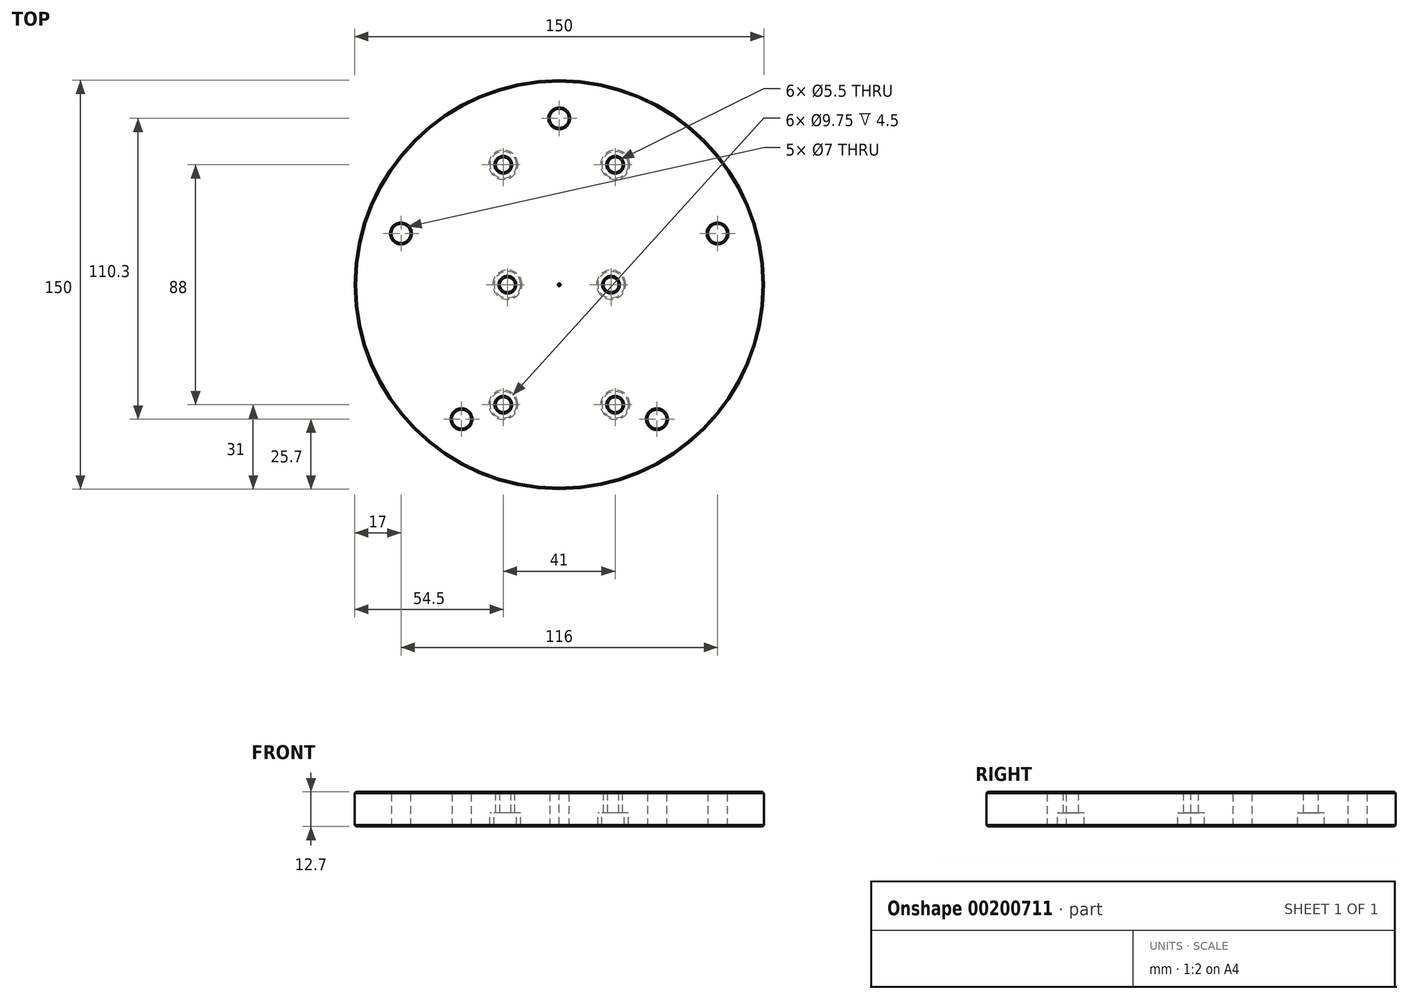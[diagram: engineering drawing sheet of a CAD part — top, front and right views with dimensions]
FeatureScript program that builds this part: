
annotation { "Feature Type Name" : "Feature", "Feature Type Description" : "" }
export const myFeature = defineFeature(function(context is Context, id is Id, definition is map)
    precondition{}
    {
        {
            var Q0;
            Q0=qCreatedBy(makeId("Top.planeOp"),FACE);
            var sketch = newSketch(context, id + "F0", { "sketchPlane" : qUnion([Q0])});
            skPoint(sketch, "E0.middle", {"position": v(0, 0) * mm});
            skCircle(sketch, "E1", {"center": v(0, 0) * mm, "radius": 75 * mm});
            skLineSegment(sketch, "E2.bottom", {"start": v(20.5, -44) * mm, "end": v(-20.5, -44) * mm, "construction": true});
            skLineSegment(sketch, "E2.top", {"start": v(20.5, 44) * mm, "end": v(-20.5, 44) * mm, "construction": true});
            skLineSegment(sketch, "E2.left", {"start": v(20.5, -44) * mm, "end": v(20.5, 44) * mm, "construction": true});
            skLineSegment(sketch, "E2.right", {"start": v(-20.5, -44) * mm, "end": v(-20.5, 44) * mm, "construction": true});
            skPoint(sketch, "E3", {"position": v(-20.5, 44) * mm});
            skPoint(sketch, "E4", {"position": v(20.5, 44) * mm});
            skPoint(sketch, "E5", {"position": v(-20.5, -44) * mm});
            skPoint(sketch, "E6", {"position": v(20.5, -44) * mm});
            skPoint(sketch, "E7", {"position": v(19, 0) * mm});
            skPoint(sketch, "E8", {"position": v(-19, 0) * mm});
            skSolve(sketch);
        }
        {
            var Q0;
            Q0=makeQuery(id+"F0.imprint","IMPRINT",FACE,{"disambiguationData":[TD([[makeQuery(id+"F0.imprint","IMPRINT",EDGE,{"derivedFrom":sQuery(id+"F0.wireOp",EDGE,"E1")}),1.0]])]});
            extrude(context, id + "F1", {"entities" : qUnion([Q0]), "depth" : 12.7 * mm});
        }
        {
            var Q0;
            Q0=sQuery(id+"F0.wireOp",VERTEX,"E3");
            var Q1;
            Q1=sQuery(id+"F0.wireOp",VERTEX,"E2.left.end");
            var Q2;
            Q2=sQuery(id+"F0.wireOp",VERTEX,"E8");
            var Q3;
            Q3=sQuery(id+"F0.wireOp",VERTEX,"E7");
            var Q4;
            Q4=sQuery(id+"F0.wireOp",VERTEX,"E5");
            var Q5;
            Q5=sQuery(id+"F0.wireOp",VERTEX,"E6");
            var Q6;
            Q6=makeQuery(id+"F1.opExtrude","SWEPT_BODY",BODY,{"disambiguationData":[OSD([sQuery(id+"F0.wireOp",EDGE,"E1")])]});
            hole(context, id + "F2", {"style" : HoleStyle.C_BORE, "endStyle" : HoleEndStyle.THROUGH, "oppositeDirection" : true, "standardTappedOrClearance" : lookupTablePath({ "standard" : "ISO", "fit" : "Normal", "size" : "M5", "type" : "Clearance" }), "standardBlindInLast" : lookupTablePath({ "fit" : "Standard", "standard" : "ISO", "size" : "M5", "type" : "Clearance" }), "holeDiameter" : 5.5 * mm, "cBoreDiameter" : 9.75 * mm, "cBoreDepth" : 5 * mm, "locations" : qUnion([Q0, Q1, Q2, Q3, Q4, Q5]), "scope" : qUnion([Q6]), "tappedDepth" : 12 * mm, "tapClearance" : 3, "startStyle" : HoleStartStyle.SKETCH});
        }
        {
            var Q0;
            Q0=makeQuery(id+"F1.opExtrude","CAP_FACE",FACE,{"disambiguationData":[OSD([sQuery(id+"F0.wireOp",EDGE,"E1")])],"isStart":false});
            var sketch = newSketch(context, id + "F3", { "sketchPlane" : qUnion([Q0])});
            skPoint(sketch, "E9", {"position": v(0, 61) * mm});
            skPoint(sketch, "E10", {"position": v(-58, 18.8) * mm});
            skPoint(sketch, "E11", {"position": v(58, 18.8) * mm});
            skPoint(sketch, "E12", {"position": v(-35.8, -49.3) * mm});
            skPoint(sketch, "E13", {"position": v(35.8, -49.3) * mm});
            skSolve(sketch);
        }
        {
            var Q0;
            Q0=sQuery(id+"F3.wireOp",VERTEX,"E9");
            var Q1;
            Q1=sQuery(id+"F3.wireOp",VERTEX,"E11");
            var Q2;
            Q2=sQuery(id+"F3.wireOp",VERTEX,"E10");
            var Q3;
            Q3=sQuery(id+"F3.wireOp",VERTEX,"E12");
            var Q4;
            Q4=sQuery(id+"F3.wireOp",VERTEX,"E13");
            var Q5;
            Q5=makeQuery(id+"F1.opExtrude","SWEPT_BODY",BODY,{"disambiguationData":[OSD([sQuery(id+"F0.wireOp",EDGE,"E1")])]});
            hole(context, id + "F4", {"style" : HoleStyle.SIMPLE, "endStyle" : HoleEndStyle.THROUGH, "standardTappedOrClearance" : lookupTablePath({ "standard" : "ISO", "engagement" : "75%", "pitch" : "1 mm", "size" : "M8", "type" : "Tapped" }), "standardBlindInLast" : lookupTablePath({ "standard" : "ISO", "engagement" : "75%", "pitch" : "1 mm", "size" : "M8", "type" : "Tapped" }), "holeDiameter" : 7 * mm, "locations" : qUnion([Q0, Q1, Q2, Q3, Q4]), "scope" : qUnion([Q5]), "isTappedThrough" : true, "majorDiameter" : 8 * mm, "showTappedDepth" : true, "startStyle" : HoleStartStyle.SKETCH});
        }
        {
            var Q0;
            Q0=sQuery(id+"F0.wireOp",VERTEX,"E0.middle");
            var Q1;
            Q1=makeQuery(id+"F1.opExtrude","SWEPT_BODY",BODY,{"disambiguationData":[OSD([sQuery(id+"F0.wireOp",EDGE,"E1")])]});
            hole(context, id + "F5", {"style" : HoleStyle.SIMPLE, "endStyle" : HoleEndStyle.THROUGH, "oppositeDirection" : true, "standardTappedOrClearance" : lookupTablePath({ "standard" : "ANSI", "size" : "5/16 (0.31)", "type" : "Drilled" }), "standardBlindInLast" : lookupTablePath({ "standard" : "ANSI", "size" : "5/16", "type" : "Drilled" }), "holeDiameter" : 5 / 406.4 * mm, "locations" : qUnion([Q0]), "scope" : qUnion([Q1]), "isTappedThrough" : true, "startStyle" : HoleStartStyle.SKETCH});
        }
        {
            var Q0;
            Q0=makeQuery(id+"F1.opExtrude","CAP_FACE",FACE,{"disambiguationData":[OSD([sQuery(id+"F0.wireOp",EDGE,"E1")])],"isStart":true});
            var Q1;
            Q1=makeQuery(id+"F1.opExtrude","CAP_FACE",FACE,{"disambiguationData":[OSD([sQuery(id+"F0.wireOp",EDGE,"E1")])],"isStart":false});
            chamfer(context, id + "F6", {"entities" : qUnion([Q0, Q1]), "width" : .5 * mm, "tangentPropagation" : true});
        }
    });
